# Revit family: Emergency_Equipment-Haws_Corporation-Tempering_Booth_8785
name_source: partatom
category: Plumbing Fixtures
revit_build: Autodesk Revit 2018 (Build: 20170223_1515(x64)
units: mm (PartAtom-declared; Revit-internal decimal feet)

## family parameters
Always vertical = Yes
Cut with Voids When Loaded = No
OmniClass Number = 23.65.35.11
OmniClass Title = Supply Water Heaters
Part Type = Normal
Room Calculation Point = No
Round Connector Dimension = Use Diameter
Shared = No
Work Plane-Based = No

## types (4) — shared parameters
Apparent Load = 480 VA
Assembly Code = G3010100
CW Connection = Yes
Connection Diameter = 1 1/4"
Depth = 60"
Description = All-Weather Emergency Water Tempering Booth
Edition number = 1
Finish = Metal - Haws Corporation - Green
HW Connection = No
Height = 102 3/4"
Keynote = S12
Manufacturer = Haws Corporation
Model = 8785
Number of Poles = 1
Phase = 3
Power Factor = 1
Product Guid = 9094f2b4-95d2-4d21-b948-cdcaf2c8640d
Product data url = https://bimobject.com
Sanitary Diameter = 2 3/4"
Supply Diameter = 1 1/2"
URL = https://www.hawsco.com
Vent Connection = No
Voltage = 480 V
Waste Connection = Yes
Width = 60"

## per-type parameters (varying)
| type | Constraints | Type Comments |
| 8785 - 119 Gallon | 1 | 119 Gallon Hot Water Storage Tank |
| 8785 - 120 Gallon | 2 | 120 Gallon Hot Water Storage Tank |
| 8785 - 330 Gallon | 3 | 330 Gallon Hot Water Storage Tank |
| 8785 - 200 Gallon | 4 | 200 Gallon Hot Water Storage Tank |

## geometry (parser evidence)
native form markers: Sweep x3
no freeform markers — native parametric forms only
